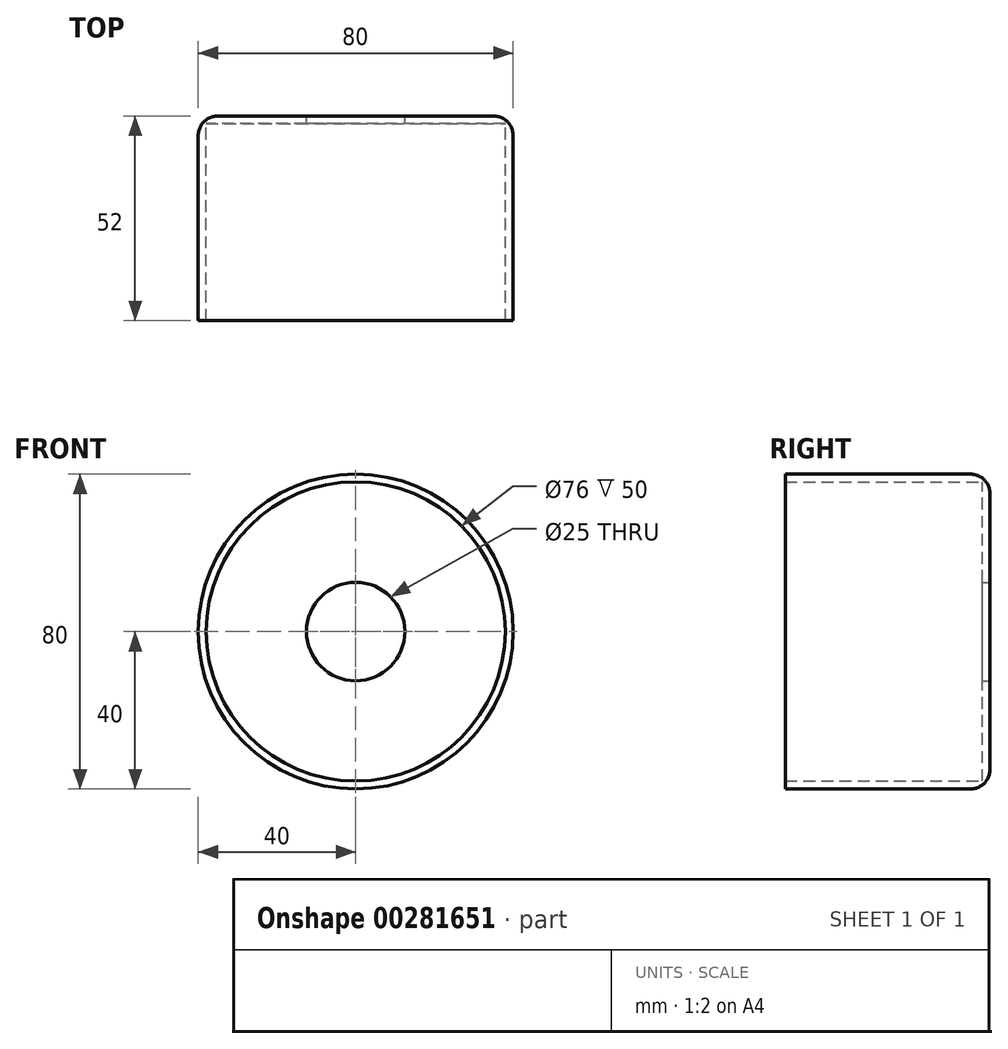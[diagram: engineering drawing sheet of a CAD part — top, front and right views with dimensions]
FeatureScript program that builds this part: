
annotation { "Feature Type Name" : "Feature", "Feature Type Description" : "" }
export const myFeature = defineFeature(function(context is Context, id is Id, definition is map)
    precondition{}
    {
        {
            var Q0;
            Q0=qCreatedBy(makeId("Front.planeOp"),FACE);
            var sketch = newSketch(context, id + "F0", { "sketchPlane" : qUnion([Q0])});
            skCircle(sketch, "E0", {"center": v(0, 0) * mm, "radius": 38 * mm});
            skSolve(sketch);
        }
        {
            var Q0;
            Q0 = qSketchRegion(id + "F0", true);
            extrude(context, id + "F1", {"entities" : qUnion([Q0]), "depth" : 50 * mm});
        }
        {
            var Q0;
            Q0=makeQuery(id+"F1.opExtrude","CAP_FACE",FACE,{"disambiguationData":[OSD([sQuery(id+"F0.wireOp",EDGE,"E0")])],"isStart":false});
            shell(context, id + "F2", {"entities" : qUnion([Q0]), "thickness" : 2 * mm, "oppositeDirection" : true});
        }
        {
            var Q0;
            Q0=makeQuery(id+"F1.opExtrude","CAP_FACE",FACE,{"disambiguationData":[OSD([sQuery(id+"F0.wireOp",EDGE,"E0")])],"isStart":true});
            var sketch = newSketch(context, id + "F3", { "sketchPlane" : qUnion([Q0])});
            skCircle(sketch, "E1", {"center": v(0, 0) * mm, "radius": 12.5 * mm});
            skSolve(sketch);
        }
        {
            var Q0;
            Q0=makeQuery(id+"F3.imprint","IMPRINT",FACE,{"disambiguationData":[TD([[makeQuery(id+"F3.imprint","IMPRINT",EDGE,{"derivedFrom":sQuery(id+"F3.wireOp",EDGE,"E1")}),1.0]])]});
            extrude(context, id + "F4", {"entities" : qUnion([Q0]), "operationType" : NewBodyOperationType.REMOVE, "endBound" : BoundingType.THROUGH_ALL, "oppositeDirection" : true, "depth" : 25 * mm});
        }
        {
            var Q0;
            Q0=makeQuery(id+"F1.opExtrude","CAP_EDGE",EDGE,{"disambiguationData":[OSD([sQuery(id+"F0.wireOp",EDGE,"E0")])],"isStart":true});
            fillet(context, id + "F5", {"entities" : qUnion([Q0]), "radius" : 5 * mm, "tangentPropagation" : true});
        }
    });
